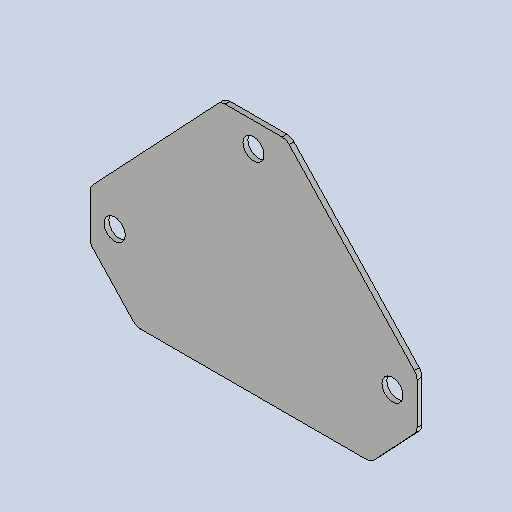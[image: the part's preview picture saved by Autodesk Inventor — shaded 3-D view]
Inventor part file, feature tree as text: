
AUTODESK INVENTOR PART (.ipt)
format: ipt  version: 2025 (Build 290162010, 162A)  size: 131,072 bytes
history: native  units: mm
features: sheet_metal_op x1, chamfer x1, sketch x1, other x1
ambient origin geometry x8: Origin, YZ Plane, XZ Plane, XY Plane, X Axis, Y Axis, Z Axis, Center Point
bodies: Solid1 (feature_tree)
feature tree (4):
  sheet_metal_op  "Face1"
  chamfer  "Corner Round2"
  sketch  "Sketch1"  dims[d2=80.0mm d3=80.0mm d6=3.0mm d17=5.0mm d18=13.0mm d19=45.0mm d20=45.0mm d21=40.0mm d22=15.0mm d23=15.0mm d24=30.0mm d25=6.0mm]
  other  "Plate1"
